# Revit family: Plumbing_Drainage_Menzies-Metal_Clamp-Tite_Copper-Box-Scupper
name_source: partatom
category: Plumbing Fixtures
revit_build: Autodesk Revit 2015 (Build: 20160512_1515(x64)
units: mm (PartAtom-declared; Revit-internal decimal feet)

## types (2) — shared parameters
Assembly Code = D2040200
Box Length = 1' - 5"
Box Length Note = Cut to suit wall depth.
Default Elevation = 4' - 0"
Description = "Clamp-Tite Copper Box Scupper"
Drain Flow = 0 GPM
Edition number = 1
Manufacturer = Menzies Metal Products
Pipe Diameter = 3"
Product Guid = 62cc6d37-6fa5-4181-b417-9199a338592b
Product Material = Metal - Menzies Metal Products - Copper
Product data url = https://bimobject.com
URL = https://www.menzies-metal.com

## per-type parameters (varying)
| type | Model | Weight |
| 3" downspout | 300-3063 | 4.40 lbf |
| 3" downspout w/ strainer kit | 300-3063 & 300-3199 | 5.00 lbf |

## geometry (parser evidence)
native form markers: Sweep x12
no freeform markers — native parametric forms only
